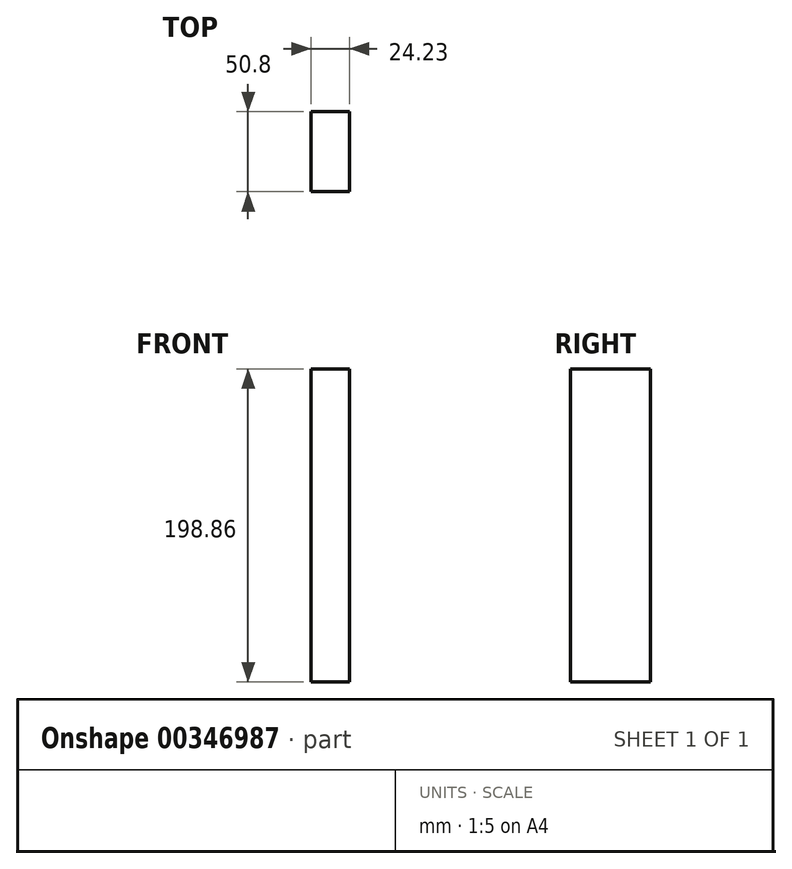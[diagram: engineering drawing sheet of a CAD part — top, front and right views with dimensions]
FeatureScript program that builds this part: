
annotation { "Feature Type Name" : "Feature", "Feature Type Description" : "" }
export const myFeature = defineFeature(function(context is Context, id is Id, definition is map)
    precondition{}
    {
        {
            var Q0;
            Q0=qCreatedBy(makeId("Front.planeOp"),FACE);
            var sketch = newSketch(context, id + "F0", { "sketchPlane" : qUnion([Q0])});
            skLineSegment(sketch, "E0.bottom", {"start": v(171.25, 130.62) * mm, "end": v(195.48, 130.62) * mm});
            skLineSegment(sketch, "E0.top", {"start": v(171.25, -68.24) * mm, "end": v(195.48, -68.24) * mm});
            skLineSegment(sketch, "E0.left", {"start": v(171.25, 130.62) * mm, "end": v(171.25, -68.24) * mm});
            skLineSegment(sketch, "E0.right", {"start": v(195.48, 130.62) * mm, "end": v(195.48, -68.24) * mm});
            skSolve(sketch);
        }
        {
            var Q0;
            Q0 = qSketchRegion(id + "F0", true);
            extrude(context, id + "F1", {"entities" : qUnion([Q0]), "depth" : 50.8 * mm, "hasSecondDirection" : true, "secondDirectionOppositeDirection" : false, "secondDirectionDepth" : 0 * mm});
        }
    });
